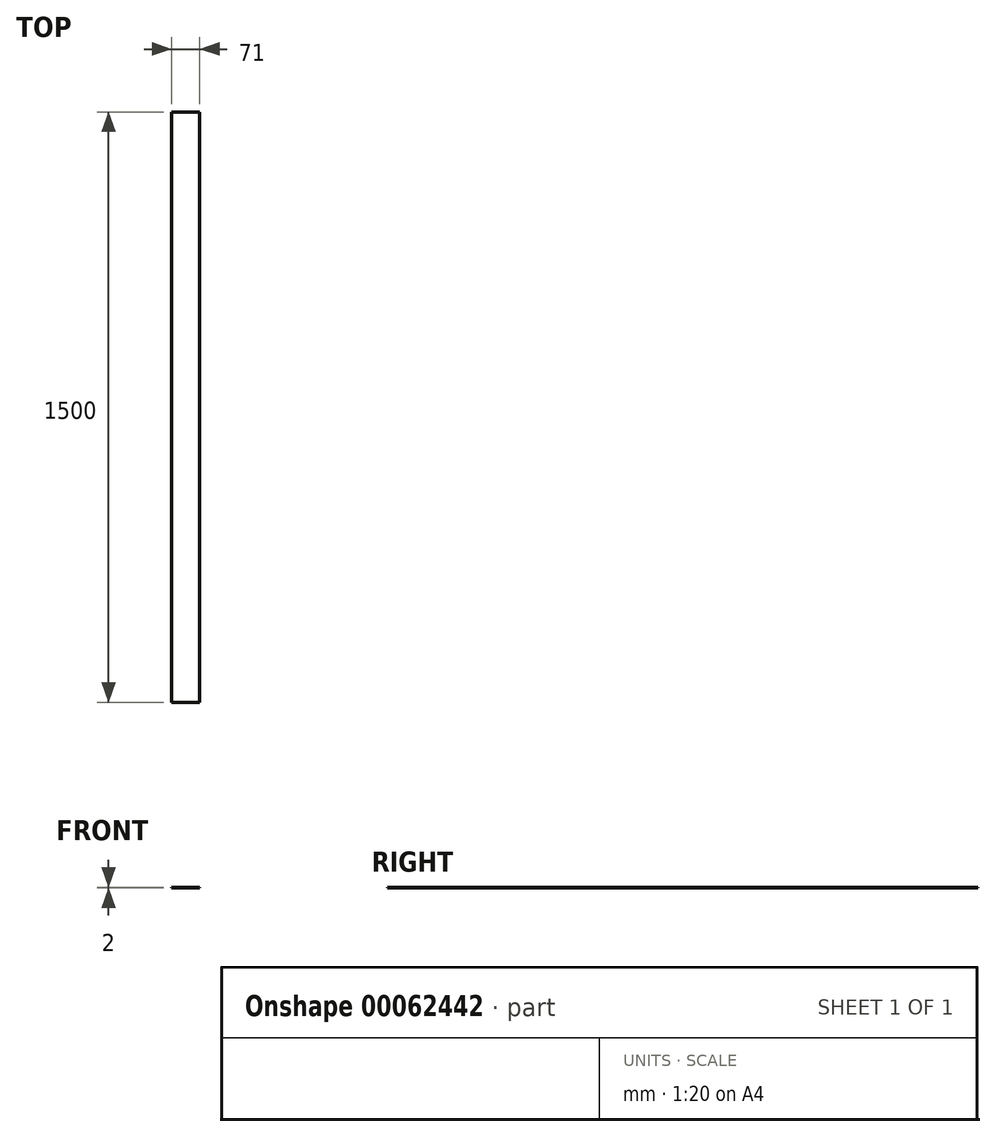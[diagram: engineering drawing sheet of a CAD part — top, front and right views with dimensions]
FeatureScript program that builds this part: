
annotation { "Feature Type Name" : "Feature", "Feature Type Description" : "" }
export const myFeature = defineFeature(function(context is Context, id is Id, definition is map)
    precondition{}
    {
        {
            var Q0;
            Q0=qCreatedBy(makeId("Front.planeOp"),FACE);
            var sketch = newSketch(context, id + "F0", { "sketchPlane" : qUnion([Q0])});
            skLineSegment(sketch, "E0.rect.bottom", {"start": v(35.5, -1) * mm, "end": v(-35.5, -1) * mm});
            skLineSegment(sketch, "E0.rect.top", {"start": v(35.5, 1) * mm, "end": v(-35.5, 1) * mm});
            skLineSegment(sketch, "E0.rect.left", {"start": v(35.5, -1) * mm, "end": v(35.5, 1) * mm});
            skLineSegment(sketch, "E0.rect.right", {"start": v(-35.5, -1) * mm, "end": v(-35.5, 1) * mm});
            skPoint(sketch, "E0.rect.middle", {"position": v(0, 0) * mm});
            skSolve(sketch);
        }
        {
            var Q0;
            Q0 = qSketchRegion(id + "F0", true);
            extrude(context, id + "F1", {"entities" : qUnion([Q0]), "endBound" : BoundingType.SYMMETRIC, "depth" : 1500 * mm});
        }
    });
